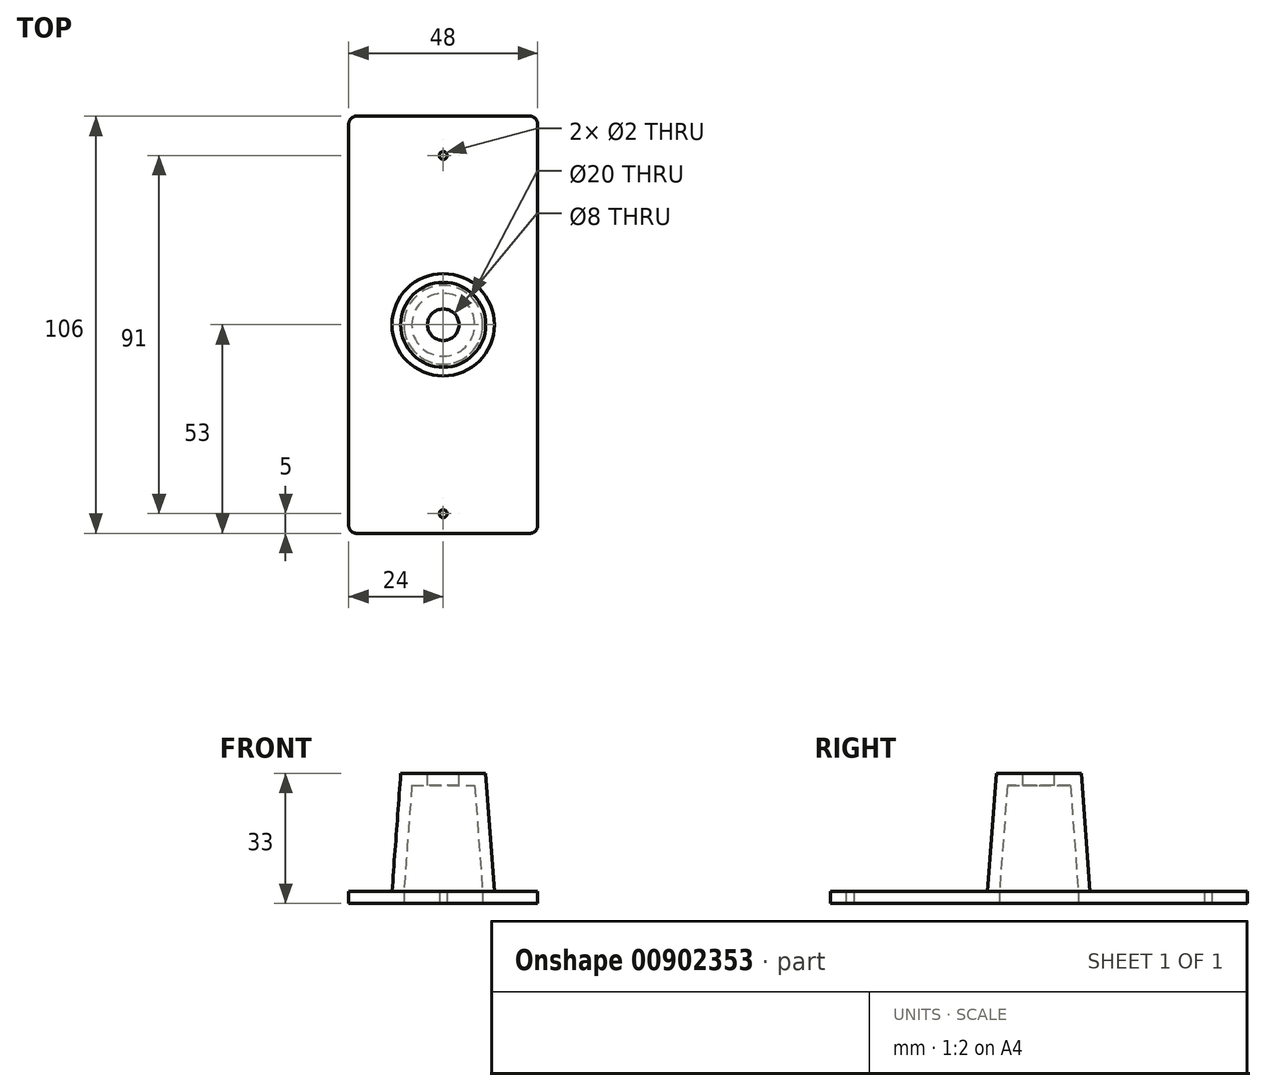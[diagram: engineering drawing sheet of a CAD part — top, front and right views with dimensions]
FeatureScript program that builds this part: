
annotation { "Feature Type Name" : "Feature", "Feature Type Description" : "" }
export const myFeature = defineFeature(function(context is Context, id is Id, definition is map)
    precondition{}
    {
        {
            var Q0;
            Q0=qCreatedBy(makeId("Top.planeOp"),FACE);
            var sketch = newSketch(context, id + "F0", { "sketchPlane" : qUnion([Q0])});
            skLineSegment(sketch, "E0.bottom", {"start": v(-22, 53) * mm, "end": v(22, 53) * mm});
            skLineSegment(sketch, "E0.top", {"start": v(-22, -53) * mm, "end": v(22, -53) * mm});
            skLineSegment(sketch, "E0.left", {"start": v(-24, 51) * mm, "end": v(-24, -51) * mm});
            skLineSegment(sketch, "E0.right", {"start": v(24, 51) * mm, "end": v(24, -51) * mm});
            skPoint(sketch, "E1.visualSharp", {"position": v(-24, 53) * mm});
            skArc(sketch, "E1.filletArc", {"start": v(-22, 53) * mm, "mid": v(-23.41, 52.41) * mm, "end": v(-24, 51) * mm});
            skPoint(sketch, "E2.visualSharp", {"position": v(24, 53) * mm});
            skArc(sketch, "E2.filletArc", {"start": v(24, 51) * mm, "mid": v(23.41, 52.41) * mm, "end": v(22, 53) * mm});
            skPoint(sketch, "E3.visualSharp", {"position": v(24, -53) * mm});
            skArc(sketch, "E3.filletArc", {"start": v(22, -53) * mm, "mid": v(23.41, -52.41) * mm, "end": v(24, -51) * mm});
            skPoint(sketch, "E4.visualSharp", {"position": v(-24, -53) * mm});
            skArc(sketch, "E4.filletArc", {"start": v(-24, -51) * mm, "mid": v(-23.41, -52.41) * mm, "end": v(-22, -53) * mm});
            skCircle(sketch, "E5", {"center": v(0, 43) * mm, "radius": 1 * mm});
            skCircle(sketch, "E6", {"center": v(0, -48) * mm, "radius": 1 * mm});
            skCircle(sketch, "E7", {"center": v(0, 0) * mm, "radius": 10 * mm});
            skSolve(sketch);
        }
        {
            var Q0;
            Q0 = qSketchRegion(id + "F0", true);
            extrude(context, id + "F1", {"entities" : qUnion([Q0]), "depth" : 3 * mm, "offsetDistance" : 25 * mm});
        }
        {
            var Q0;
            Q0=qCreatedBy(makeId("Right.planeOp"),FACE);
            var sketch = newSketch(context, id + "F2", { "sketchPlane" : qUnion([Q0])});
            skLineSegment(sketch, "E8.0", {"start": v(51, 3) * mm, "end": v(-51, 3) * mm, "construction": true});
            skLineSegment(sketch, "E9", {"start": v(10, 3) * mm, "end": v(8, 30) * mm});
            skLineSegment(sketch, "E10", {"start": v(-10, 3) * mm, "end": v(-13.1, 3) * mm});
            skLineSegment(sketch, "E11", {"start": v(10.79, 33) * mm, "end": v(13, 3) * mm});
            skLineSegment(sketch, "E12", {"start": v(13, 3) * mm, "end": v(10, 3) * mm});
            skLineSegment(sketch, "E13", {"start": v(8, 30) * mm, "end": v(0, 30) * mm});
            skLineSegment(sketch, "E14", {"start": v(0, 30) * mm, "end": v(0, 33) * mm});
            skLineSegment(sketch, "E15", {"start": v(0, 33) * mm, "end": v(10.79, 33) * mm});
            skLineSegment(sketch, "E16", {"start": v(0, 0.96) * mm, "end": v(0, 7.7) * mm, "construction": true});
            skSolve(sketch);
        }
        {
            var Q0;
            Q0 = qSketchRegion(id + "F2", true);
            var Q1;
            Q1=sQuery(id+"F2.wireOp",EDGE,"E16");
            revolve(context, id + "F3", {"operationType" : NewBodyOperationType.ADD, "surfaceOperationType" : NewSurfaceOperationType.NEW, "entities" : qUnion([Q0]), "axis" : qUnion([Q1]), "revolveType" : RevolveType.FULL});
        }
        {
            var Q0;
            Q0=makeQuery(id+"F3.opRevolve","SWEPT_FACE",FACE,{"disambiguationData":[OSD([sQuery(id+"F2.wireOp",EDGE,"E15")])]});
            var sketch = newSketch(context, id + "F4", { "sketchPlane" : qUnion([Q0])});
            skCircle(sketch, "E17", {"center": v(0, 0) * mm, "radius": 4 * mm});
            skSolve(sketch);
        }
        {
            var Q0;
            Q0 = qSketchRegion(id + "F4", true);
            extrude(context, id + "F5", {"entities" : qUnion([Q0]), "operationType" : NewBodyOperationType.REMOVE, "endBound" : BoundingType.THROUGH_ALL, "oppositeDirection" : true, "depth" : 25 * mm, "offsetDistance" : 25 * mm});
        }
    });
